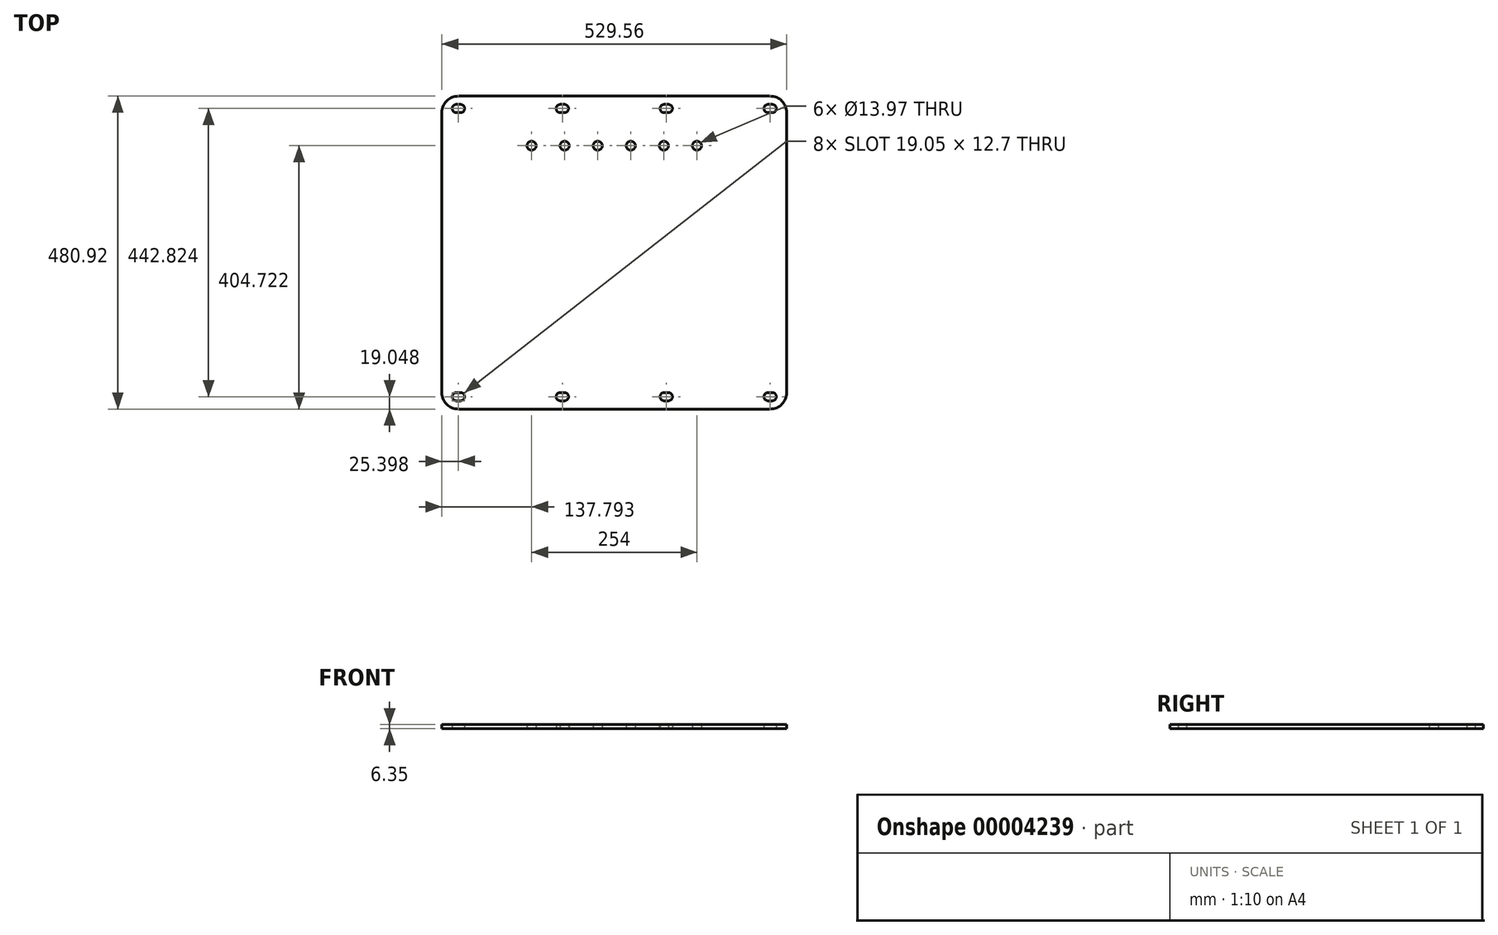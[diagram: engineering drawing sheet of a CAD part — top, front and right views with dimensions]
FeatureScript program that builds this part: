
annotation { "Feature Type Name" : "Feature", "Feature Type Description" : "" }
export const myFeature = defineFeature(function(context is Context, id is Id, definition is map)
    precondition{}
    {
        {
            var Q0;
            Q0=qCreatedBy(makeId("Top.planeOp"),FACE);
            var sketch = newSketch(context, id + "F0", { "sketchPlane" : qUnion([Q0])});
            skLineSegment(sketch, "E0.rect.bottom", {"start": v(239.38, 240.46) * mm, "end": v(-239.38, 240.46) * mm});
            skLineSegment(sketch, "E0.rect.top", {"start": v(239.38, -240.46) * mm, "end": v(-239.38, -240.46) * mm});
            skLineSegment(sketch, "E0.rect.left", {"start": v(264.78, 215.06) * mm, "end": v(264.78, -215.06) * mm});
            skLineSegment(sketch, "E0.rect.right", {"start": v(-264.78, 215.06) * mm, "end": v(-264.78, -215.06) * mm});
            skPoint(sketch, "E0.rect.middle", {"position": v(0, 0) * mm});
            skLineSegment(sketch, "E1", {"start": v(-239.38, 221.41) * mm, "end": v(-79.8, 221.41) * mm, "construction": true});
            skLineSegment(sketch, "E2", {"start": v(-79.8, 221.41) * mm, "end": v(79.8, 221.41) * mm, "construction": true});
            skLineSegment(sketch, "E3", {"start": v(79.8, 221.41) * mm, "end": v(239.38, 221.41) * mm, "construction": true});
            skLineSegment(sketch, "E4", {"start": v(-239.38, -221.41) * mm, "end": v(-79.8, -221.41) * mm, "construction": true});
            skLineSegment(sketch, "E5", {"start": v(-79.8, -221.41) * mm, "end": v(79.8, -221.41) * mm, "construction": true});
            skLineSegment(sketch, "E6", {"start": v(79.8, -221.41) * mm, "end": v(239.38, -221.41) * mm, "construction": true});
            skPoint(sketch, "E7.visualSharp", {"position": v(-264.78, 240.46) * mm});
            skArc(sketch, "E7.filletArc", {"start": v(-239.38, 240.46) * mm, "mid": v(-257.34, 233.02) * mm, "end": v(-264.78, 215.06) * mm});
            skPoint(sketch, "E8.visualSharp", {"position": v(264.78, 240.46) * mm});
            skArc(sketch, "E8.filletArc", {"start": v(264.78, 215.06) * mm, "mid": v(257.34, 233.02) * mm, "end": v(239.38, 240.46) * mm});
            skPoint(sketch, "E9.visualSharp", {"position": v(264.78, -240.46) * mm});
            skArc(sketch, "E9.filletArc", {"start": v(239.38, -240.46) * mm, "mid": v(257.34, -233.02) * mm, "end": v(264.78, -215.06) * mm});
            skPoint(sketch, "E10.visualSharp", {"position": v(-264.78, -240.46) * mm});
            skArc(sketch, "E10.filletArc", {"start": v(-264.78, -215.06) * mm, "mid": v(-257.34, -233.02) * mm, "end": v(-239.38, -240.46) * mm});
            skLineSegment(sketch, "E11", {"start": v(-242.56, 227.76) * mm, "end": v(-236.2, 227.76) * mm});
            skLineSegment(sketch, "E12", {"start": v(-242.56, 215.06) * mm, "end": v(-236.2, 215.06) * mm});
            skLineSegment(sketch, "E13", {"start": v(-82.97, 227.76) * mm, "end": v(-76.62, 227.76) * mm});
            skLineSegment(sketch, "E14", {"start": v(-82.97, 215.06) * mm, "end": v(-76.62, 215.06) * mm});
            skLineSegment(sketch, "E15", {"start": v(76.62, 227.76) * mm, "end": v(82.97, 227.76) * mm});
            skLineSegment(sketch, "E16", {"start": v(76.62, 215.06) * mm, "end": v(82.97, 215.06) * mm});
            skLineSegment(sketch, "E17", {"start": v(236.2, 227.76) * mm, "end": v(242.56, 227.76) * mm});
            skLineSegment(sketch, "E18", {"start": v(236.2, 215.06) * mm, "end": v(242.56, 215.06) * mm});
            skLineSegment(sketch, "E19", {"start": v(-242.56, -215.06) * mm, "end": v(-236.2, -215.06) * mm});
            skLineSegment(sketch, "E20", {"start": v(-82.97, -215.06) * mm, "end": v(-76.62, -215.06) * mm});
            skLineSegment(sketch, "E21", {"start": v(76.62, -215.06) * mm, "end": v(82.97, -215.06) * mm});
            skLineSegment(sketch, "E22", {"start": v(236.2, -215.06) * mm, "end": v(242.56, -215.06) * mm});
            skLineSegment(sketch, "E23", {"start": v(-242.56, -227.76) * mm, "end": v(-236.2, -227.76) * mm});
            skLineSegment(sketch, "E24", {"start": v(-82.97, -227.76) * mm, "end": v(-76.62, -227.76) * mm});
            skLineSegment(sketch, "E25", {"start": v(76.62, -227.76) * mm, "end": v(82.97, -227.76) * mm});
            skLineSegment(sketch, "E26", {"start": v(236.2, -227.76) * mm, "end": v(242.56, -227.76) * mm});
            skArc(sketch, "E27", {"start": v(-242.56, 227.76) * mm, "mid": v(-248.9, 221.41) * mm, "end": v(-242.56, 215.06) * mm});
            skArc(sketch, "E28", {"start": v(-236.2, 215.06) * mm, "mid": v(-229.86, 221.41) * mm, "end": v(-236.2, 227.76) * mm});
            skArc(sketch, "E29", {"start": v(-82.97, 227.76) * mm, "mid": v(-89.32, 221.41) * mm, "end": v(-82.97, 215.06) * mm});
            skArc(sketch, "E30", {"start": v(-76.62, 215.06) * mm, "mid": v(-70.27, 221.41) * mm, "end": v(-76.62, 227.76) * mm});
            skArc(sketch, "E31", {"start": v(76.62, 227.76) * mm, "mid": v(70.27, 221.41) * mm, "end": v(76.62, 215.06) * mm});
            skArc(sketch, "E32", {"start": v(82.97, 215.06) * mm, "mid": v(89.32, 221.41) * mm, "end": v(82.97, 227.76) * mm});
            skArc(sketch, "E33", {"start": v(236.2, 227.76) * mm, "mid": v(229.86, 221.41) * mm, "end": v(236.2, 215.06) * mm});
            skArc(sketch, "E34", {"start": v(242.56, 215.06) * mm, "mid": v(248.9, 221.41) * mm, "end": v(242.56, 227.76) * mm});
            skArc(sketch, "E35", {"start": v(242.56, -227.76) * mm, "mid": v(248.9, -221.41) * mm, "end": v(242.56, -215.06) * mm});
            skArc(sketch, "E36", {"start": v(236.2, -215.06) * mm, "mid": v(229.86, -221.41) * mm, "end": v(236.2, -227.76) * mm});
            skArc(sketch, "E37", {"start": v(82.97, -227.76) * mm, "mid": v(89.32, -221.41) * mm, "end": v(82.97, -215.06) * mm});
            skArc(sketch, "E38", {"start": v(76.62, -215.06) * mm, "mid": v(70.27, -221.41) * mm, "end": v(76.62, -227.76) * mm});
            skArc(sketch, "E39", {"start": v(-76.62, -227.76) * mm, "mid": v(-70.27, -221.41) * mm, "end": v(-76.62, -215.06) * mm});
            skArc(sketch, "E40", {"start": v(-82.97, -215.06) * mm, "mid": v(-89.32, -221.41) * mm, "end": v(-82.97, -227.76) * mm});
            skArc(sketch, "E41", {"start": v(-236.2, -227.76) * mm, "mid": v(-229.86, -221.41) * mm, "end": v(-236.2, -215.06) * mm});
            skArc(sketch, "E42", {"start": v(-242.56, -215.06) * mm, "mid": v(-248.9, -221.41) * mm, "end": v(-242.56, -227.76) * mm});
            skCircle(sketch, "E43", {"center": v(-126.99, 164.26) * mm, "radius": 6.99 * mm});
            skCircle(sketch, "E44.1.0.0", {"center": v(-76.19, 164.26) * mm, "radius": 6.99 * mm});
            skCircle(sketch, "E44.2.0.0", {"center": v(-25.39, 164.26) * mm, "radius": 6.99 * mm});
            skCircle(sketch, "E44.3.0.0", {"center": v(25.41, 164.26) * mm, "radius": 6.99 * mm});
            skLineSegment(sketch, "E44.direction1", {"start": v(-126.99, 164.26) * mm, "end": v(-76.19, 164.26) * mm, "construction": true});
            skCircle(sketch, "E45.0.4.0", {"center": v(76.21, 164.26) * mm, "radius": 6.99 * mm});
            skCircle(sketch, "E45.0.5.0", {"center": v(127.01, 164.26) * mm, "radius": 6.99 * mm});
            skSolve(sketch);
        }
        {
            var Q0;
            Q0 = qSketchRegion(id + "F0", true);
            extrude(context, id + "F1", {"entities" : qUnion([Q0]), "depth" : 6.35 * mm});
        }
    });
